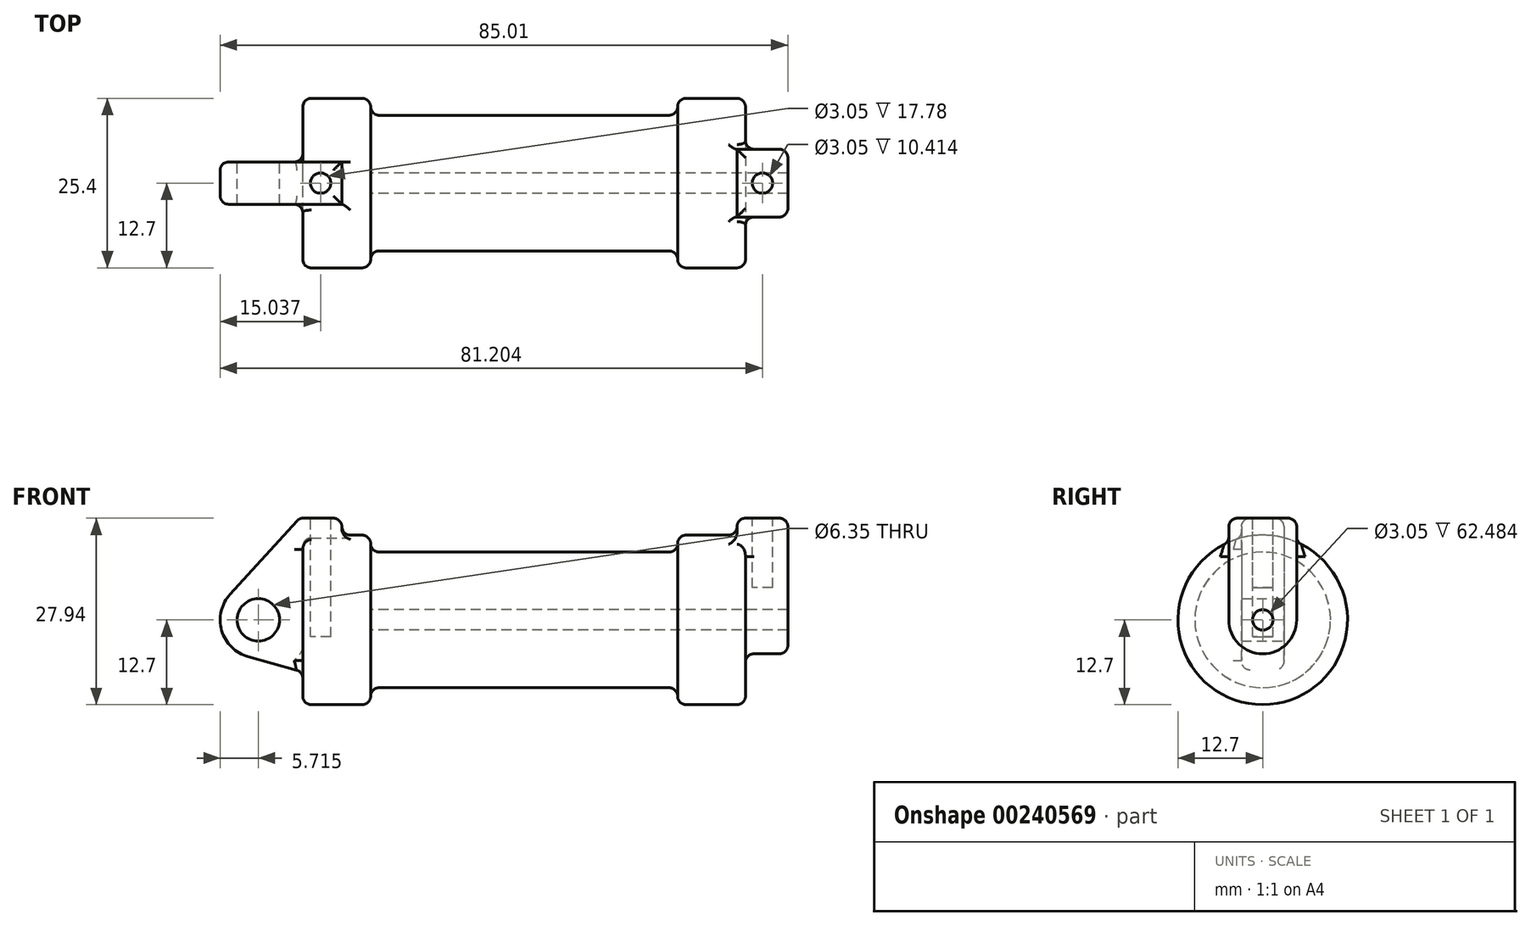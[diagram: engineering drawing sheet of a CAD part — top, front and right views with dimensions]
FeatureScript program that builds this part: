
annotation { "Feature Type Name" : "Feature", "Feature Type Description" : "" }
export const myFeature = defineFeature(function(context is Context, id is Id, definition is map)
    precondition{}
    {
        {
            var Q0;
            Q0=qCreatedBy(makeId("Front.planeOp"),FACE);
            var sketch = newSketch(context, id + "F0", { "sketchPlane" : qUnion([Q0])});
            skLineSegment(sketch, "E0", {"start": v(0, 0) * mm, "end": v(0, 12.7) * mm});
            skLineSegment(sketch, "E1", {"start": v(0, 12.7) * mm, "end": v(10.16, 12.7) * mm});
            skLineSegment(sketch, "E2", {"start": v(10.16, 12.7) * mm, "end": v(10.16, 10.16) * mm});
            skLineSegment(sketch, "E3", {"start": v(10.16, 10.16) * mm, "end": v(56.13, 10.16) * mm});
            skLineSegment(sketch, "E4", {"start": v(56.13, 10.16) * mm, "end": v(56.13, 12.7) * mm});
            skLineSegment(sketch, "E5", {"start": v(56.13, 12.7) * mm, "end": v(66.3, 12.7) * mm});
            skLineSegment(sketch, "E6", {"start": v(66.3, 12.7) * mm, "end": v(66.3, 0) * mm});
            skLineSegment(sketch, "E7", {"start": v(66.3, 0) * mm, "end": v(0, 0) * mm});
            skLineSegment(sketch, "E8", {"start": v(5.84, 15.24) * mm, "end": v(-0.5, 15.24) * mm});
            skLineSegment(sketch, "E9", {"start": v(-0.5, 15.24) * mm, "end": v(-10.88, 3.85) * mm});
            skLineSegment(sketch, "E10", {"start": v(0, 0) * mm, "end": v(-6.65, 0) * mm});
            skCircle(sketch, "E11", {"center": v(-6.65, 0) * mm, "radius": 5.72 * mm});
            skCircle(sketch, "E12", {"center": v(-6.65, 0) * mm, "radius": 3.18 * mm});
            skLineSegment(sketch, "E13", {"start": v(5.84, 15.24) * mm, "end": v(5.84, -9.4) * mm});
            skLineSegment(sketch, "E14", {"start": v(5.84, -9.4) * mm, "end": v(-8.18, -5.5) * mm});
            skSolve(sketch);
        }
        {
            var Q0;
            {var subQ0=sQuery(id+"F0.wireOp",EDGE,"E0");Q0=makeQuery(id+"F0.imprint","IMPRINT",FACE,{"disambiguationData":[TD([[makeQuery(id+"F0.imprint","IMPRINT",EDGE,{"derivedFrom":subQ0}),-1.0]])]});}
            var Q1;
            {var subQ0=sQuery(id+"F0.wireOp",EDGE,"E2");Q1=makeQuery(id+"F0.imprint","IMPRINT",FACE,{"disambiguationData":[TD([[makeQuery(id+"F0.imprint","IMPRINT",EDGE,{"derivedFrom":subQ0}),-1.0]])]});}
            var Q2;
            Q2=sQuery(id+"F0.wireOp",EDGE,"E7");
            revolve(context, id + "F1", {"entities" : qUnion([Q0, Q1]), "axis" : qUnion([Q2]), "revolveType" : RevolveType.FULL});
        }
        {
            var Q0;
            {var subQ4=sQuery(id+"F0.wireOp",EDGE,"E12");Q0=makeQuery(id+"F0.imprint","IMPRINT",FACE,{"disambiguationData":[TD([[makeQuery(id+"F0.imprint","IMPRINT",EDGE,{"derivedFrom":subQ4}),-1.0]])]});}
            var Q1;
            {var subQ0=sQuery(id+"F0.wireOp",EDGE,"E14");Q1=makeQuery(id+"F0.imprint","IMPRINT",FACE,{"disambiguationData":[TD([[makeQuery(id+"F0.imprint","IMPRINT",EDGE,{"derivedFrom":subQ0}),-1.0]])]});}
            var Q2;
            {var subQ0=sQuery(id+"F0.wireOp",EDGE,"E0");Q2=makeQuery(id+"F0.imprint","IMPRINT",FACE,{"disambiguationData":[TD([[makeQuery(id+"F0.imprint","IMPRINT",EDGE,{"derivedFrom":subQ0}),-1.0]])]});}
            var Q3;
            {var subQ3=sQuery(id+"F0.wireOp",EDGE,"E0");Q3=makeQuery(id+"F0.imprint","IMPRINT",FACE,{"disambiguationData":[TD([[makeQuery(id+"F0.imprint","IMPRINT",EDGE,{"derivedFrom":subQ3}),1.0]])]});}
            extrude(context, id + "F2", {"entities" : qUnion([Q0, Q1, Q2, Q3]), "operationType" : NewBodyOperationType.ADD, "endBound" : BoundingType.SYMMETRIC, "depth" : 6.35 * mm});
        }
        {
            var Q0;
            Q0=makeQuery(id+"F1.opRevolve","SWEPT_FACE",FACE,{"disambiguationData":[OSD([sQuery(id+"F0.wireOp",EDGE,"E6")])]});
            var sketch = newSketch(context, id + "F3", { "sketchPlane" : qUnion([Q0])});
            skCircle(sketch, "E15", {"center": v(0, 0) * mm, "radius": 1.52 * mm});
            skCircle(sketch, "E16", {"center": v(0, 0) * mm, "radius": 5.08 * mm});
            skLineSegment(sketch, "E17", {"start": v(-5.08, 0) * mm, "end": v(-5.08, 15.24) * mm});
            skLineSegment(sketch, "E18", {"start": v(-5.08, 15.24) * mm, "end": v(5.08, 15.24) * mm});
            skLineSegment(sketch, "E19", {"start": v(5.08, 15.24) * mm, "end": v(5.08, 0) * mm});
            skSolve(sketch);
        }
        {
            var Q0;
            Q0 = qSketchRegion(id + "F3", true);
            extrude(context, id + "F4", {"entities" : qUnion([Q0]), "operationType" : NewBodyOperationType.ADD, "depth" : 6.35 * mm, "hasSecondDirection" : true, "secondDirectionOppositeDirection" : true, "secondDirectionDepth" : 1.27 * mm});
        }
        {
            var Q0;
            Q0=makeQuery(id+"F3.imprint","IMPRINT",FACE,{"disambiguationData":[TD([[makeQuery(id+"F3.imprint","IMPRINT",EDGE,{"derivedFrom":sQuery(id+"F3.wireOp",EDGE,"E15")}),1.0]])]});
            var Q1;
            Q1=makeQuery(id+"F1.opRevolve","SWEPT_FACE",FACE,{"disambiguationData":[OSD([sQuery(id+"F0.wireOp",EDGE,"E2")])]});
            extrude(context, id + "F5", {"entities" : qUnion([Q0]), "operationType" : NewBodyOperationType.REMOVE, "endBound" : BoundingType.UP_TO_SURFACE, "oppositeDirection" : true, "endBoundEntityFace" : qUnion([Q1]), "depth" : 25.4 * mm});
        }
        {
            var Q0;
            Q0=makeQuery(id+"F2.opExtrude","SWEPT_FACE",FACE,{"disambiguationData":[OSD([sQuery(id+"F0.wireOp",EDGE,"E8")])]});
            var sketch = newSketch(context, id + "F6", { "sketchPlane" : qUnion([Q0])});
            skCircle(sketch, "E20", {"center": v(2.67, 0) * mm, "radius": 1.52 * mm});
            skPoint(sketch, "E20.centerSnap0", {"position": v(2.67, -3.18) * mm});
            skPoint(sketch, "E20.centerSnap1", {"position": v(5.84, 0) * mm});
            skSolve(sketch);
        }
        {
            var Q0;
            Q0 = qSketchRegion(id + "F6", true);
            extrude(context, id + "F7", {"entities" : qUnion([Q0]), "operationType" : NewBodyOperationType.REMOVE, "oppositeDirection" : true, "depth" : 17.78 * mm});
        }
        {
            var Q0;
            Q0=makeQuery(id+"F4.opExtrude","SWEPT_FACE",FACE,{"disambiguationData":[OSD([sQuery(id+"F3.wireOp",EDGE,"E18")])]});
            var sketch = newSketch(context, id + "F8", { "sketchPlane" : qUnion([Q0])});
            skCircle(sketch, "E21", {"center": v(68.83, 0) * mm, "radius": 1.52 * mm});
            skPoint(sketch, "E21.centerSnap0", {"position": v(68.83, -5.08) * mm});
            skPoint(sketch, "E21.centerSnap1", {"position": v(65.02, 0) * mm});
            skSolve(sketch);
        }
        {
            var Q0;
            Q0=makeQuery(id+"F8.imprint","IMPRINT",FACE,{"disambiguationData":[TD([[makeQuery(id+"F8.imprint","IMPRINT",EDGE,{"derivedFrom":sQuery(id+"F8.wireOp",EDGE,"E21")}),1.0]])]});
            extrude(context, id + "F9", {"entities" : qUnion([Q0]), "operationType" : NewBodyOperationType.REMOVE, "oppositeDirection" : true, "depth" : 10.4 * mm});
        }
        {
            var Q0;
            Q0=makeQuery(id+"F1.opRevolve","SWEPT_EDGE",EDGE,{"disambiguationData":[OSD([sQuery(id+"F0.wireOp",EDGE,"E0"),sQuery(id+"F0.wireOp",EDGE,"E1")])]});
            var Q1;
            Q1=makeQuery(id+"F1.opRevolve","SWEPT_EDGE",EDGE,{"disambiguationData":[OSD([sQuery(id+"F0.wireOp",EDGE,"E1"),sQuery(id+"F0.wireOp",EDGE,"E2")])]});
            var Q2;
            Q2=makeQuery(id+"F1.opRevolve","SWEPT_EDGE",EDGE,{"disambiguationData":[OSD([sQuery(id+"F0.wireOp",EDGE,"E2"),sQuery(id+"F0.wireOp",EDGE,"E3")])]});
            var Q3;
            Q3=makeQuery(id+"F1.opRevolve","SWEPT_EDGE",EDGE,{"disambiguationData":[OSD([sQuery(id+"F0.wireOp",EDGE,"E5"),sQuery(id+"F0.wireOp",EDGE,"E6")])]});
            var Q4;
            Q4=makeQuery(id+"F1.opRevolve","SWEPT_EDGE",EDGE,{"disambiguationData":[OSD([sQuery(id+"F0.wireOp",EDGE,"E4"),sQuery(id+"F0.wireOp",EDGE,"E5")])]});
            var Q5;
            Q5=makeQuery(id+"F1.opRevolve","SWEPT_EDGE",EDGE,{"disambiguationData":[OSD([sQuery(id+"F0.wireOp",EDGE,"E3"),sQuery(id+"F0.wireOp",EDGE,"E4")])]});
            fillet(context, id + "F10", {"entities" : qUnion([Q0, Q1, Q2, Q3, Q4, Q5]), "radius" : 1.27 * mm, "tangentPropagation" : true, "allowEdgeOverflow" : false});
        }
        {
            var Q0;
            Q0=makeQuery(id+"F2.boolean.opBoolean","INTERSECT",EDGE,{"derivedFrom":[makeQuery(id+"F1.opRevolve","SWEPT_FACE",FACE,{"disambiguationData":[OSD([sQuery(id+"F0.wireOp",EDGE,"E0")])]}),makeQuery(id+"F2.opExtrude","SWEPT_FACE",FACE,{"disambiguationData":[OSD([sQuery(id+"F0.wireOp",EDGE,"E14")])]})]});
            var Q1;
            Q1=makeQuery(id+"F2.boolean.opBoolean","INTERSECT",EDGE,{"derivedFrom":[makeQuery(id+"F1.opRevolve","SWEPT_FACE",FACE,{"disambiguationData":[OSD([sQuery(id+"F0.wireOp",EDGE,"E0")])]}),makeQuery(id+"F2.opExtrude","CAP_FACE",FACE,{"disambiguationData":[OSD([sQuery(id+"F0.wireOp",EDGE,"E8"),sQuery(id+"F0.wireOp",EDGE,"E9"),sQuery(id+"F0.wireOp",EDGE,"E11"),sQuery(id+"F0.wireOp",EDGE,"E12"),sQuery(id+"F0.wireOp",EDGE,"E13"),sQuery(id+"F0.wireOp",EDGE,"E14")])],"isStart":false})]});
            var Q2;
            Q2=makeQuery(id+"F2.opExtrude","CAP_EDGE",EDGE,{"disambiguationData":[OSD([sQuery(id+"F0.wireOp",EDGE,"E14")])],"isStart":false});
            var Q3;
            Q3=makeQuery(id+"F2.opExtrude","CAP_EDGE",EDGE,{"disambiguationData":[OSD([sQuery(id+"F0.wireOp",EDGE,"E14")])],"isStart":true});
            var Q4;
            Q4=makeQuery(id+"F2.opExtrude","SWEPT_EDGE",EDGE,{"disambiguationData":[OSD([sQuery(id+"F0.wireOp",EDGE,"E8"),sQuery(id+"F0.wireOp",EDGE,"E9")])]});
            var Q5;
            Q5=makeQuery(id+"F2.opExtrude","CAP_EDGE",EDGE,{"disambiguationData":[OSD([sQuery(id+"F0.wireOp",EDGE,"E8")])],"isStart":true});
            var Q6;
            Q6=makeQuery(id+"F2.opExtrude","SWEPT_EDGE",EDGE,{"disambiguationData":[OSD([sQuery(id+"F0.wireOp",EDGE,"E8"),sQuery(id+"F0.wireOp",EDGE,"E13")])]});
            var Q7;
            Q7=makeQuery(id+"F2.opExtrude","CAP_EDGE",EDGE,{"disambiguationData":[OSD([sQuery(id+"F0.wireOp",EDGE,"E8")])],"isStart":false});
            var Q8;
            Q8=makeQuery(id+"F2.boolean.opBoolean","INTERSECT",EDGE,{"derivedFrom":[makeQuery(id+"F1.opRevolve","SWEPT_FACE",FACE,{"disambiguationData":[OSD([sQuery(id+"F0.wireOp",EDGE,"E1")])]}),makeQuery(id+"F2.opExtrude","SWEPT_FACE",FACE,{"disambiguationData":[OSD([sQuery(id+"F0.wireOp",EDGE,"E13")])]})]});
            fillet(context, id + "F11", {"entities" : qUnion([Q0, Q1, Q2, Q3, Q4, Q5, Q6, Q7, Q8]), "radius" : 1.27 * mm, "tangentPropagation" : true, "allowEdgeOverflow" : false});
        }
        {
            var Q0;
            Q0=makeQuery(id+"F4.boolean.opBoolean","INTERSECT",EDGE,{"derivedFrom":[makeQuery(id+"F1.opRevolve","SWEPT_FACE",FACE,{"disambiguationData":[OSD([sQuery(id+"F0.wireOp",EDGE,"E5")])]}),makeQuery(id+"F4.opExtrude","CAP_FACE",FACE,{"disambiguationData":[OSD([sQuery(id+"F3.wireOp",EDGE,"E15"),sQuery(id+"F3.wireOp",EDGE,"E16"),sQuery(id+"F3.wireOp",EDGE,"E17"),sQuery(id+"F3.wireOp",EDGE,"E18"),sQuery(id+"F3.wireOp",EDGE,"E19")])],"isStart":true})]});
            var Q1;
            Q1=makeQuery(id+"F4.opExtrude","CAP_EDGE",EDGE,{"disambiguationData":[OSD([sQuery(id+"F3.wireOp",EDGE,"E18")])],"isStart":true});
            var Q2;
            Q2=makeQuery(id+"F4.opExtrude","SWEPT_EDGE",EDGE,{"disambiguationData":[OSD([sQuery(id+"F3.wireOp",EDGE,"E18"),sQuery(id+"F3.wireOp",EDGE,"E19")])]});
            var Q3;
            Q3=makeQuery(id+"F4.opExtrude","CAP_EDGE",EDGE,{"disambiguationData":[OSD([sQuery(id+"F3.wireOp",EDGE,"E18")])],"isStart":false});
            var Q4;
            Q4=makeQuery(id+"F4.opExtrude","SWEPT_EDGE",EDGE,{"disambiguationData":[OSD([sQuery(id+"F3.wireOp",EDGE,"E17"),sQuery(id+"F3.wireOp",EDGE,"E18")])]});
            var Q5;
            Q5=makeQuery(id+"F10.opFillet","BLEND_EDGE",EDGE,{"blendedFrom":[makeQuery(id+"F1.opRevolve","SWEPT_EDGE",EDGE,{"disambiguationData":[OSD([sQuery(id+"F0.wireOp",EDGE,"E5"),sQuery(id+"F0.wireOp",EDGE,"E6")])]}),makeQuery(id+"F4.opExtrude","SWEPT_FACE",FACE,{"disambiguationData":[OSD([sQuery(id+"F3.wireOp",EDGE,"E17")])]})],"blendedInto":[makeQuery(id+"F4.opExtrude","SWEPT_FACE",FACE,{"disambiguationData":[OSD([sQuery(id+"F3.wireOp",EDGE,"E17")])]})]});
            var Q6;
            Q6=makeQuery(id+"F4.opExtrude","CAP_EDGE",EDGE,{"disambiguationData":[OSD([sQuery(id+"F3.wireOp",EDGE,"E17")])],"isStart":false});
            fillet(context, id + "F12", {"entities" : qUnion([Q0, Q1, Q2, Q3, Q4, Q5, Q6]), "radius" : 1.27 * mm, "tangentPropagation" : true, "allowEdgeOverflow" : false});
        }
    });
